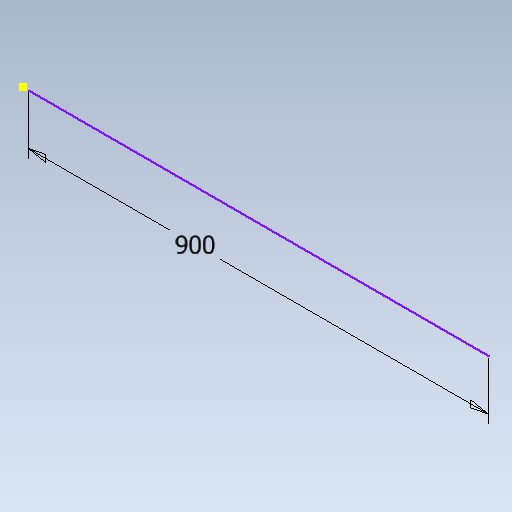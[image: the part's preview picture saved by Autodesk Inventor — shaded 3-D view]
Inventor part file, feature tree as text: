
AUTODESK INVENTOR PART (.ipt)
format: ipt  version: 2020.1 (Build 241239000, 239)  size: 83,968 bytes
history: native  units: mm
features: sketch x1
ambient origin geometry x8: Origin, YZ Plane, XZ Plane, XY Plane, X Axis, Y Axis, Z Axis, Center Point
feature tree (1):
  sketch  "Sketch1"  dims[d0=900.0mm]
